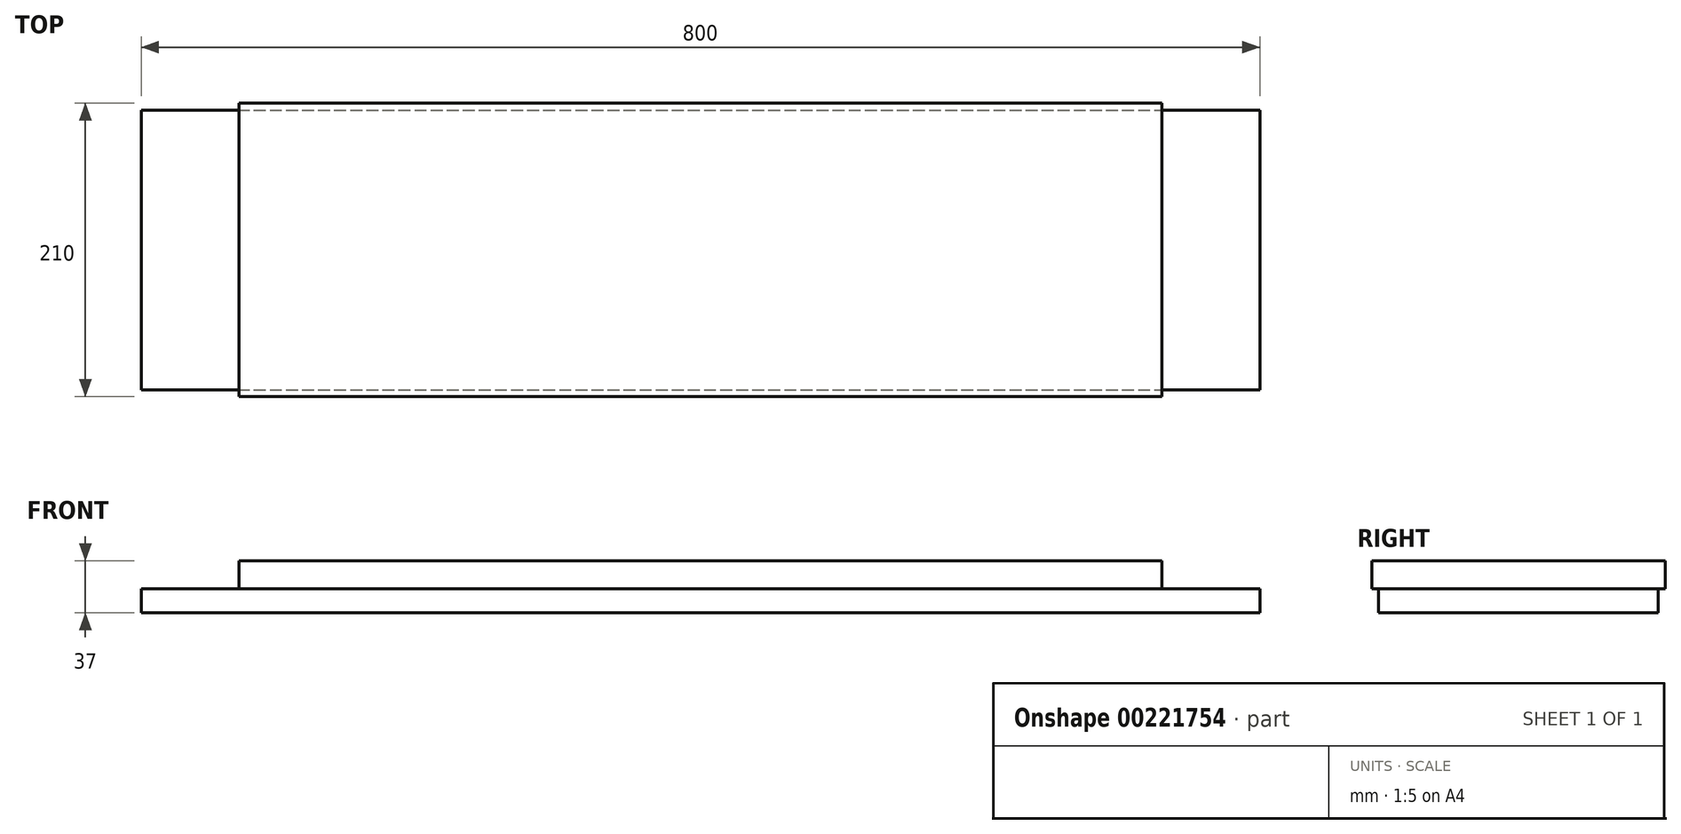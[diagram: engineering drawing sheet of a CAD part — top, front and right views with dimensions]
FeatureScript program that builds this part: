
annotation { "Feature Type Name" : "Feature", "Feature Type Description" : "" }
export const myFeature = defineFeature(function(context is Context, id is Id, definition is map)
    precondition{}
    {
        {
            var Q0;
            Q0=qCreatedBy(makeId("Top.planeOp"),FACE);
            var sketch = newSketch(context, id + "F0", { "sketchPlane" : qUnion([Q0])});
            skLineSegment(sketch, "E0.bottom", {"start": v(-330, 105) * mm, "end": v(330, 105) * mm});
            skLineSegment(sketch, "E0.top", {"start": v(-330, -105) * mm, "end": v(330, -105) * mm});
            skLineSegment(sketch, "E0.left", {"start": v(-330, 105) * mm, "end": v(-330, -105) * mm});
            skLineSegment(sketch, "E0.right", {"start": v(330, 105) * mm, "end": v(330, -105) * mm});
            skPoint(sketch, "E0.middle", {"position": v(0, 0) * mm});
            skSolve(sketch);
        }
        {
            var Q0;
            Q0 = qSketchRegion(id + "F0", true);
            extrude(context, id + "F1", {"entities" : qUnion([Q0]), "depth" : 20 * mm});
        }
        {
            var Q0;
            Q0=makeQuery(id+"F1.opExtrude","CAP_FACE",FACE,{"disambiguationData":[OSD([sQuery(id+"F0.wireOp",EDGE,"E0.bottom"),sQuery(id+"F0.wireOp",EDGE,"E0.top"),sQuery(id+"F0.wireOp",EDGE,"E0.left"),sQuery(id+"F0.wireOp",EDGE,"E0.right")])],"isStart":true});
            var sketch = newSketch(context, id + "F2", { "sketchPlane" : qUnion([Q0])});
            skLineSegment(sketch, "E1.bottom", {"start": v(-400, 100) * mm, "end": v(400, 100) * mm});
            skLineSegment(sketch, "E1.top", {"start": v(-400, -100) * mm, "end": v(400, -100) * mm});
            skLineSegment(sketch, "E1.left", {"start": v(-400, 100) * mm, "end": v(-400, -100) * mm});
            skLineSegment(sketch, "E1.right", {"start": v(400, 100) * mm, "end": v(400, -100) * mm});
            skPoint(sketch, "E1.middle", {"position": v(0, 0) * mm});
            skSolve(sketch);
        }
        {
            var Q0;
            Q0 = qSketchRegion(id + "F2", true);
            extrude(context, id + "F3", {"entities" : qUnion([Q0]), "depth" : 17 * mm});
        }
    });
